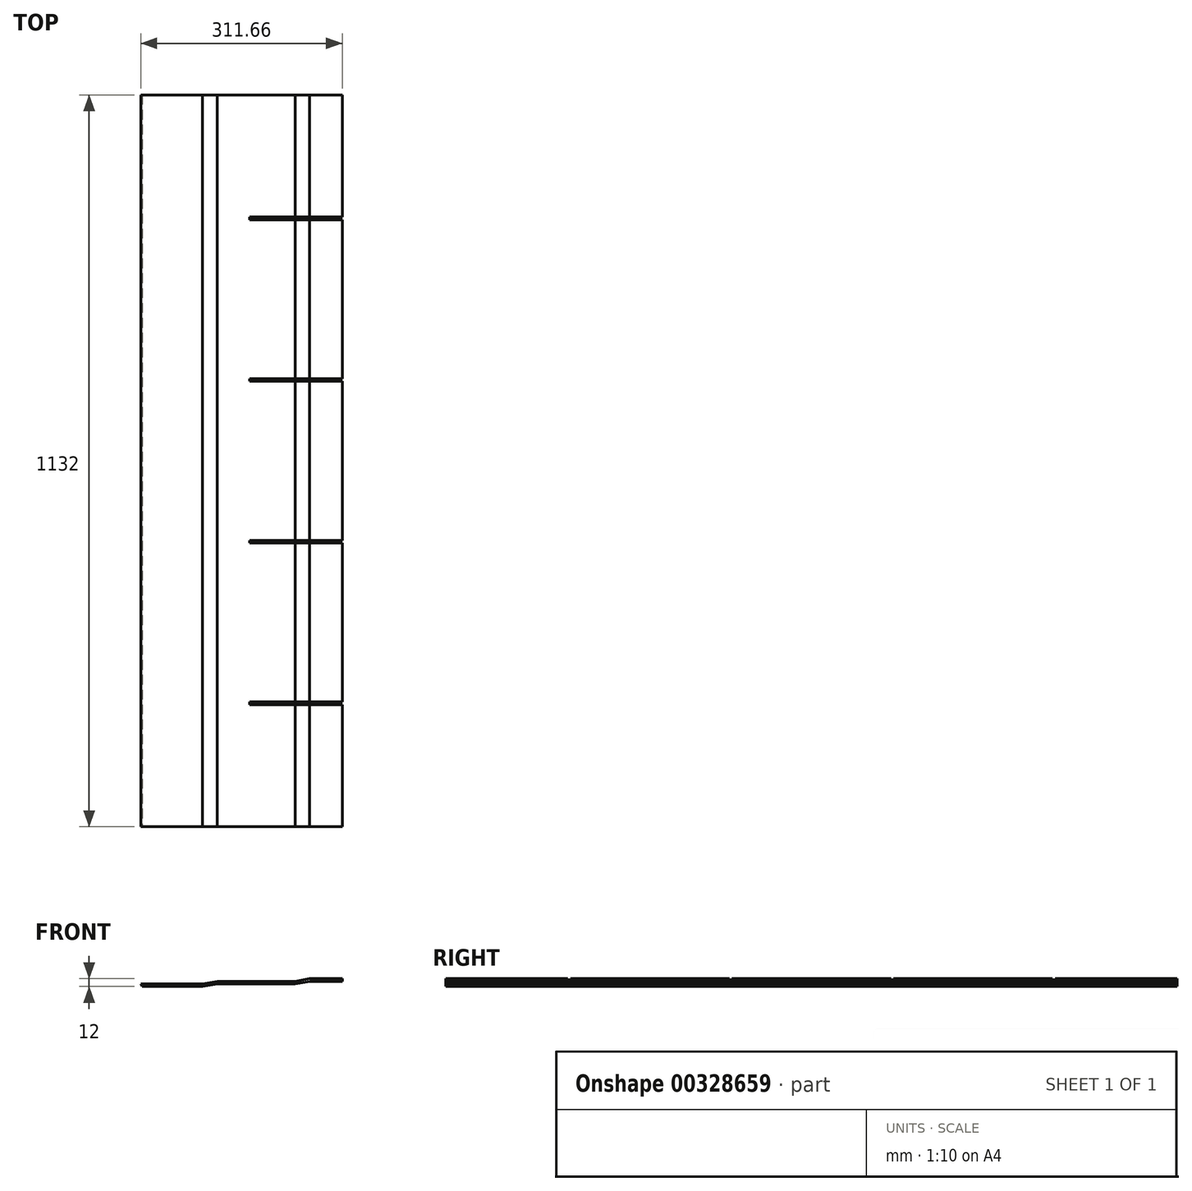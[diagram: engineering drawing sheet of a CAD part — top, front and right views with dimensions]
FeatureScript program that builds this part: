
annotation { "Feature Type Name" : "Feature", "Feature Type Description" : "" }
export const myFeature = defineFeature(function(context is Context, id is Id, definition is map)
    precondition{}
    {
        {
            var Q0;
            Q0=qCreatedBy(makeId("Front.planeOp"),FACE);
            var sketch = newSketch(context, id + "F0", { "sketchPlane" : qUnion([Q0])});
            skLineSegment(sketch, "E0.bottom", {"start": v(0, 0) * mm, "end": v(95.62, 0) * mm});
            skLineSegment(sketch, "E0.top", {"start": v(1.66, -4) * mm, "end": v(95.97, -4) * mm});
            skLineSegment(sketch, "E1", {"start": v(311.66, 4) * mm, "end": v(261.66, 4) * mm});
            skLineSegment(sketch, "E2", {"start": v(118.3, 4) * mm, "end": v(95.62, 0) * mm});
            skLineSegment(sketch, "E3", {"start": v(118.66, 0) * mm, "end": v(95.97, -4) * mm});
            skLineSegment(sketch, "E4.trimOffspring", {"start": v(118.66, 0) * mm, "end": v(238.97, 0) * mm});
            skLineSegment(sketch, "E5", {"start": v(311.66, 4) * mm, "end": v(311.66, 8) * mm});
            skLineSegment(sketch, "E6", {"start": v(311.66, 8) * mm, "end": v(261.3, 8) * mm});
            skLineSegment(sketch, "E7", {"start": v(261.3, 8) * mm, "end": v(238.62, 4) * mm});
            skLineSegment(sketch, "E8", {"start": v(238.97, 0) * mm, "end": v(261.66, 4) * mm});
            skLineSegment(sketch, "E9.trimOffspring", {"start": v(238.62, 4) * mm, "end": v(118.3, 4) * mm});
            skLineSegment(sketch, "E10", {"start": v(1.66, -4) * mm, "end": v(0, 0) * mm});
            skSolve(sketch);
        }
        {
            var Q0;
            Q0=qSketchRegion(id+"F0",true);
            extrude(context, id + "F1", {"entities" : qUnion([Q0]), "oppositeDirection" : true, "depth" : 1132 * mm});
        }
        {
            var Q0;
            Q0=makeQuery(id+"F1.opExtrude","SWEPT_FACE",FACE,{"disambiguationData":[OSD([sQuery(id+"F0.wireOp",EDGE,"E9.trimOffspring")])]});
            var sketch = newSketch(context, id + "F2", { "sketchPlane" : qUnion([Q0])});
            skLineSegment(sketch, "E11", {"start": v(168.66, 189) * mm, "end": v(168.66, 193) * mm});
            skLineSegment(sketch, "E12", {"start": v(168.66, 193) * mm, "end": v(311.66, 193) * mm});
            skLineSegment(sketch, "E13", {"start": v(311.66, 193) * mm, "end": v(311.66, 189) * mm});
            skLineSegment(sketch, "E14", {"start": v(311.66, 189) * mm, "end": v(168.66, 189) * mm});
            skLineSegment(sketch, "E15.0.1.0", {"start": v(311.66, 443) * mm, "end": v(311.66, 439) * mm});
            skLineSegment(sketch, "E15.0.1.1", {"start": v(168.66, 439) * mm, "end": v(168.66, 443) * mm});
            skLineSegment(sketch, "E15.0.1.2", {"start": v(168.66, 443) * mm, "end": v(311.66, 443) * mm});
            skLineSegment(sketch, "E15.0.1.3", {"start": v(311.66, 439) * mm, "end": v(168.66, 439) * mm});
            skLineSegment(sketch, "E15.0.2.0", {"start": v(311.66, 693) * mm, "end": v(311.66, 689) * mm});
            skLineSegment(sketch, "E15.0.2.1", {"start": v(168.66, 689) * mm, "end": v(168.66, 693) * mm});
            skLineSegment(sketch, "E15.0.2.2", {"start": v(168.66, 693) * mm, "end": v(311.66, 693) * mm});
            skLineSegment(sketch, "E15.0.2.3", {"start": v(311.66, 689) * mm, "end": v(168.66, 689) * mm});
            skLineSegment(sketch, "E15.direction1", {"start": v(168.66, 189) * mm, "end": v(193, 189) * mm, "construction": true});
            skLineSegment(sketch, "E15.direction2", {"start": v(168.66, 189) * mm, "end": v(168.66, 439) * mm, "construction": true});
            skLineSegment(sketch, "E16.0.0.3", {"start": v(311.66, 943) * mm, "end": v(311.66, 939) * mm});
            skLineSegment(sketch, "E16.3.0.3", {"start": v(168.66, 939) * mm, "end": v(168.66, 943) * mm});
            skLineSegment(sketch, "E16.6.0.3", {"start": v(168.66, 943) * mm, "end": v(311.66, 943) * mm});
            skLineSegment(sketch, "E16.9.0.3", {"start": v(311.66, 939) * mm, "end": v(168.66, 939) * mm});
            skSolve(sketch);
        }
        {
            var Q0;
            Q0=qSketchRegion(id+"F2",true);
            extrude(context, id + "F3", {"entities" : qUnion([Q0]), "operationType" : NewBodyOperationType.REMOVE, "endBound" : BoundingType.THROUGH_ALL, "oppositeDirection" : true, "depth" : 25 * mm, "hasSecondDirection" : true, "secondDirectionBound" : SecondDirectionBoundingType.THROUGH_ALL, "secondDirectionOppositeDirection" : false, "secondDirectionDepth" : 25 * mm});
        }
    });
